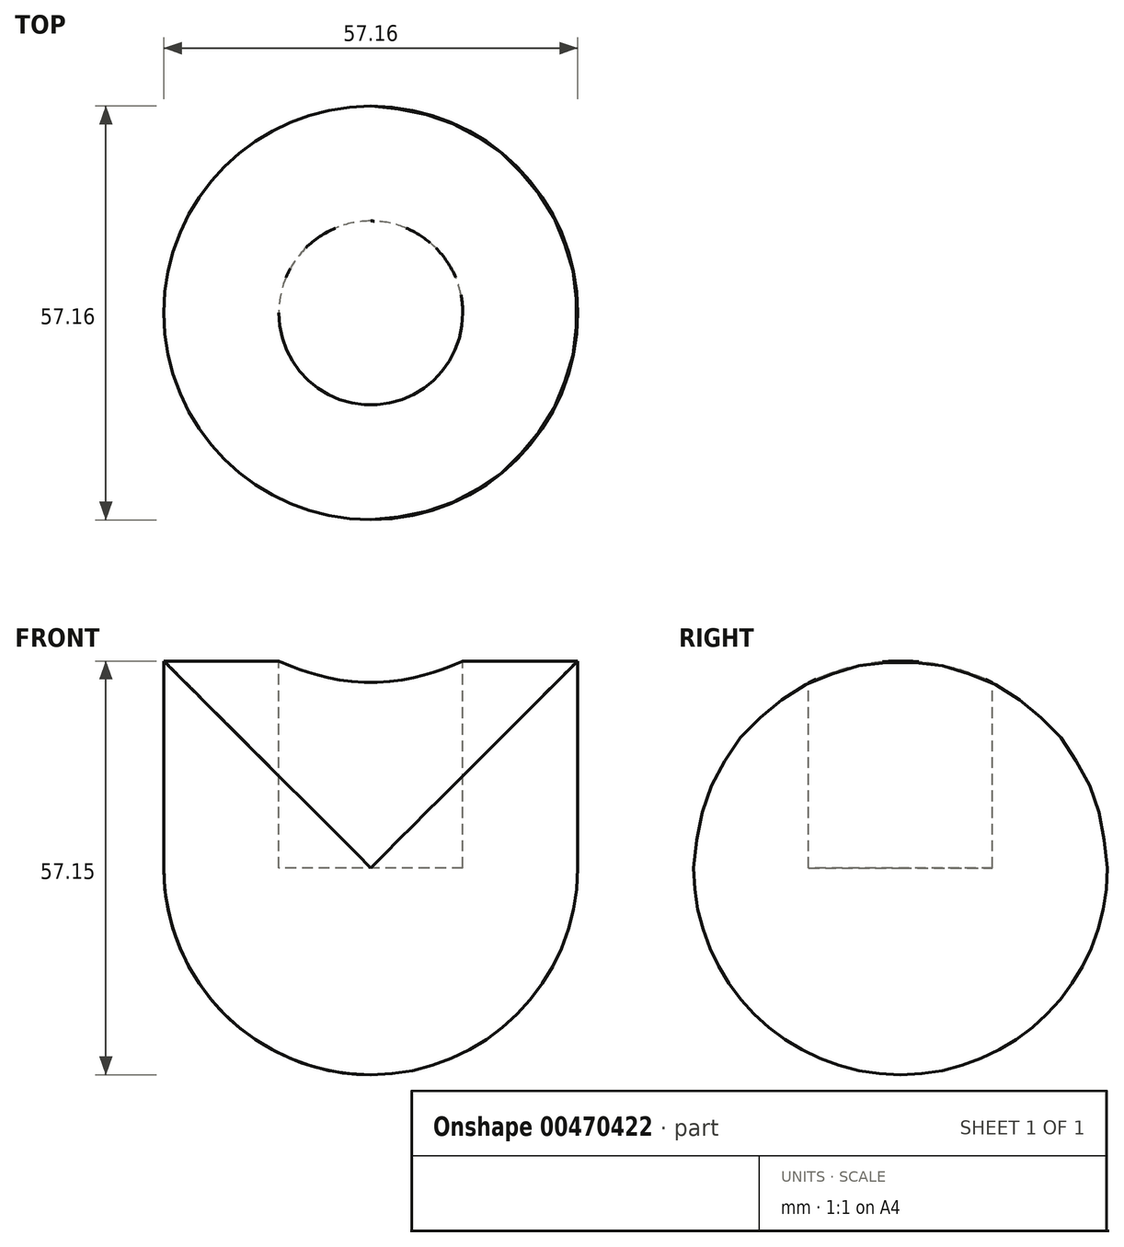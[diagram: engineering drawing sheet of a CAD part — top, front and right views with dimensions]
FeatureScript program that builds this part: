
annotation { "Feature Type Name" : "Feature", "Feature Type Description" : "" }
export const myFeature = defineFeature(function(context is Context, id is Id, definition is map)
    precondition{}
    {
        {
            var Q0;
            Q0=qCreatedBy(makeId("Front.planeOp"),FACE);
            var sketch = newSketch(context, id + "F0", { "sketchPlane" : qUnion([Q0])});
            skLineSegment(sketch, "E0.bottom", {"start": v(28.57, -28.58) * mm, "end": v(-28.58, -28.58) * mm});
            skLineSegment(sketch, "E0.top", {"start": v(28.58, 28.58) * mm, "end": v(-28.57, 28.57) * mm});
            skLineSegment(sketch, "E0.left", {"start": v(28.57, -28.58) * mm, "end": v(28.58, 28.58) * mm});
            skLineSegment(sketch, "E0.right", {"start": v(-28.58, -28.58) * mm, "end": v(-28.58, 28.57) * mm});
            skPoint(sketch, "E0.middle", {"position": v(0, 0) * mm});
            skSolve(sketch);
        }
        {
            var Q0;
            Q0=qCreatedBy(makeId("Right.planeOp"),FACE);
            var sketch = newSketch(context, id + "F1", { "sketchPlane" : qUnion([Q0])});
            skLineSegment(sketch, "E1.bottom", {"start": v(28.58, 28.58) * mm, "end": v(-28.57, 28.58) * mm});
            skLineSegment(sketch, "E1.top", {"start": v(28.57, -28.58) * mm, "end": v(-28.58, -28.58) * mm});
            skLineSegment(sketch, "E1.left", {"start": v(28.58, 28.58) * mm, "end": v(28.57, -28.58) * mm});
            skLineSegment(sketch, "E1.right", {"start": v(-28.57, 28.58) * mm, "end": v(-28.58, -28.58) * mm});
            skPoint(sketch, "E1.middle", {"position": v(0, 0) * mm});
            skSolve(sketch);
        }
        {
            var Q0;
            Q0=makeQuery(id+"F0.imprint","IMPRINT",FACE,{"disambiguationData":[TD([[makeQuery(id+"F0.imprint","IMPRINT",EDGE,{"derivedFrom":sQuery(id+"F0.wireOp",EDGE,"E0.bottom")}),-1.0]])]});
            extrude(context, id + "F2", {"entities" : qUnion([Q0]), "endBound" : BoundingType.SYMMETRIC, "depth" : 57.15 * mm});
        }
        {
            var Q0;
            Q0=makeQuery(id+"F2.opExtrude","SWEPT_FACE",FACE,{"disambiguationData":[OSD([sQuery(id+"F0.wireOp",EDGE,"E0.top")])]});
            var sketch = newSketch(context, id + "F3", { "sketchPlane" : qUnion([Q0])});
            skCircle(sketch, "E2", {"center": v(0, 0) * mm, "radius": 12.7 * mm});
            skSolve(sketch);
        }
        {
            var Q0;
            Q0=makeQuery(id+"F3.imprint","IMPRINT",FACE,{"disambiguationData":[TD([[makeQuery(id+"F3.imprint","IMPRINT",EDGE,{"derivedFrom":sQuery(id+"F3.wireOp",EDGE,"E2")}),1.0]])]});
            var sketch = newSketch(context, id + "F4", { "sketchPlane" : qUnion([Q0])});
            skSolve(sketch);
        }
        {
            var Q0;
            Q0=makeQuery(id+"F3.imprint","IMPRINT",FACE,{"disambiguationData":[TD([[makeQuery(id+"F3.imprint","IMPRINT",EDGE,{"derivedFrom":sQuery(id+"F3.wireOp",EDGE,"E2")}),1.0]])]});
            var Q1;
            Q1=qCreatedBy(makeId("Top.planeOp"),FACE);
            extrude(context, id + "F5", {"entities" : qUnion([Q0]), "operationType" : NewBodyOperationType.REMOVE, "endBound" : BoundingType.UP_TO_SURFACE, "oppositeDirection" : true, "endBoundEntityFace" : qUnion([Q1]), "depth" : 25.4 * mm});
        }
        {
            var Q0;
            Q0=makeQuery(id+"F2.opExtrude","CAP_EDGE",EDGE,{"disambiguationData":[OSD([sQuery(id+"F0.wireOp",EDGE,"E0.top")])],"isStart":false});
            var Q1;
            Q1=makeQuery(id+"F2.opExtrude","CAP_EDGE",EDGE,{"disambiguationData":[OSD([sQuery(id+"F0.wireOp",EDGE,"E0.right")])],"isStart":false});
            var Q2;
            Q2=makeQuery(id+"F2.opExtrude","CAP_EDGE",EDGE,{"disambiguationData":[OSD([sQuery(id+"F0.wireOp",EDGE,"E0.bottom")])],"isStart":false});
            var Q3;
            Q3=makeQuery(id+"F2.opExtrude","CAP_EDGE",EDGE,{"disambiguationData":[OSD([sQuery(id+"F0.wireOp",EDGE,"E0.left")])],"isStart":false});
            var Q4;
            Q4=makeQuery(id+"F2.opExtrude","SWEPT_EDGE",EDGE,{"disambiguationData":[OSD([sQuery(id+"F0.wireOp",EDGE,"E0.bottom"),sQuery(id+"F0.wireOp",EDGE,"E0.left")])]});
            var Q5;
            Q5=makeQuery(id+"F2.opExtrude","SWEPT_EDGE",EDGE,{"disambiguationData":[OSD([sQuery(id+"F0.wireOp",EDGE,"E0.bottom"),sQuery(id+"F0.wireOp",EDGE,"E0.right")])]});
            var Q6;
            Q6=makeQuery(id+"F2.opExtrude","CAP_EDGE",EDGE,{"disambiguationData":[OSD([sQuery(id+"F0.wireOp",EDGE,"E0.bottom")])],"isStart":true});
            var Q7;
            Q7=makeQuery(id+"F2.opExtrude","CAP_EDGE",EDGE,{"disambiguationData":[OSD([sQuery(id+"F0.wireOp",EDGE,"E0.right")])],"isStart":true});
            var Q8;
            Q8=makeQuery(id+"F2.opExtrude","CAP_EDGE",EDGE,{"disambiguationData":[OSD([sQuery(id+"F0.wireOp",EDGE,"E0.left")])],"isStart":true});
            var Q9;
            Q9=makeQuery(id+"F2.opExtrude","CAP_EDGE",EDGE,{"disambiguationData":[OSD([sQuery(id+"F0.wireOp",EDGE,"E0.top")])],"isStart":true});
            fillet(context, id + "F6", {"entities" : qUnion([Q0, Q1, Q2, Q3, Q4, Q5, Q6, Q7, Q8, Q9]), "radius" : 28.57 * mm, "tangentPropagation" : true, "allowEdgeOverflow" : false});
        }
    });
